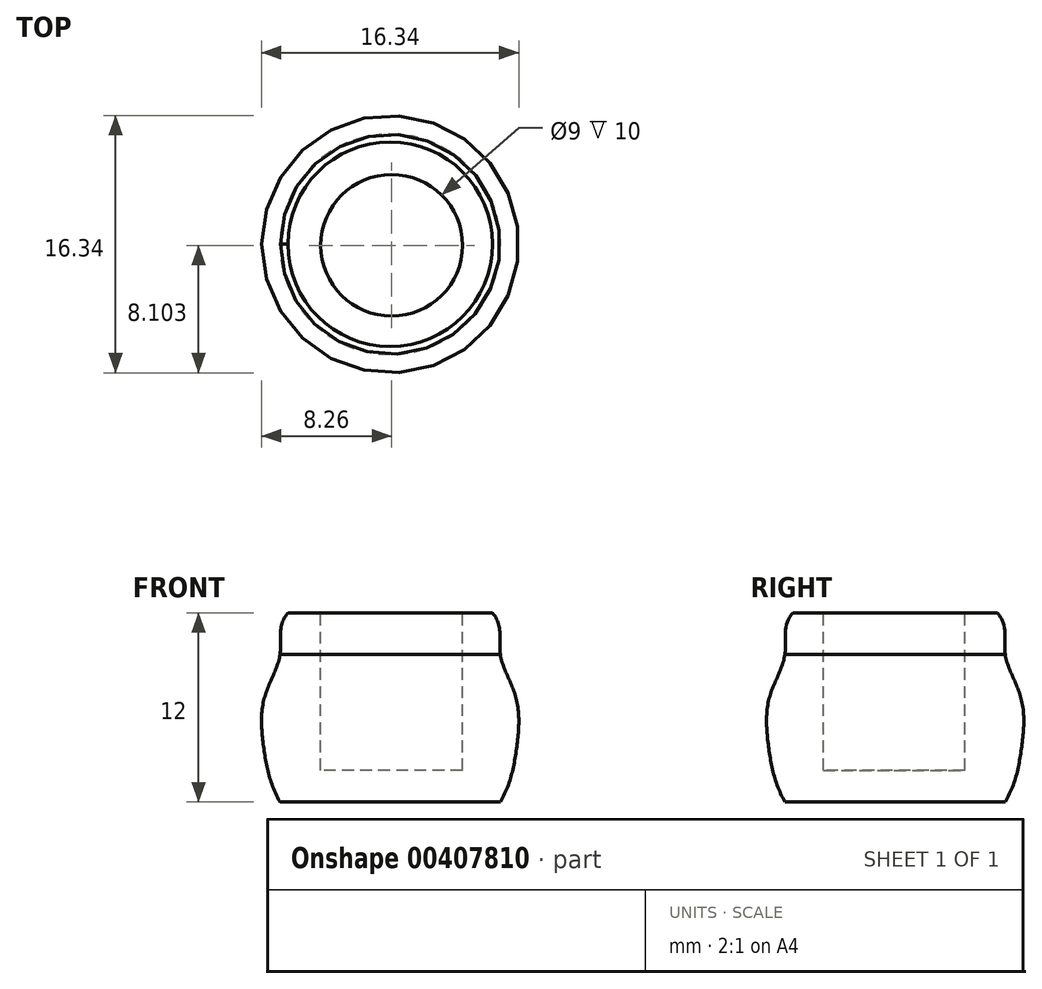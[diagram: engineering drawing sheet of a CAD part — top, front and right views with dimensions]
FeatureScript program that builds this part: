
annotation { "Feature Type Name" : "Feature", "Feature Type Description" : "" }
export const myFeature = defineFeature(function(context is Context, id is Id, definition is map)
    precondition{}
    {
        {
            var Q0;
            Q0=qCreatedBy(makeId("Front.planeOp"),FACE);
            var sketch = newSketch(context, id + "F0", { "sketchPlane" : qUnion([Q0])});
            skLineSegment(sketch, "E0", {"start": v(0, 0) * mm, "end": v(0, 12) * mm});
            skLineSegment(sketch, "E1", {"start": v(0, 0) * mm, "end": v(7, 0) * mm});
            skLineSegment(sketch, "E2", {"start": v(0, 12) * mm, "end": v(6.5, 12) * mm});
            skLineSegment(sketch, "E3", {"start": v(0, 6.58) * mm, "end": v(8, 6.58) * mm});
            skLineSegment(sketch, "E4", {"start": v(0, 3.23) * mm, "end": v(8, 3.23) * mm});
            skLineSegment(sketch, "E5", {"start": v(0, 9.37) * mm, "end": v(7, 9.37) * mm});
            skFitSpline(sketch, "E6", {"points": [v(6.5, 12) * mm, v(7, 9.37) * mm, v(8, 6.58) * mm, v(8, 3.23) * mm, v(7, 0) * mm], "startDerivative": vector(9.14, -10.6) * mm, "endDerivative": vector(-7.15, -12.58) * mm});
            skSolve(sketch);
        }
        {
            var Q0;
            Q0 = qSketchRegion(id + "F0", true);
            var Q1;
            Q1=sQuery(id+"F0.wireOp",EDGE,"E0");
            revolve(context, id + "F1", {"entities" : qUnion([Q0]), "axis" : qUnion([Q1]), "revolveType" : RevolveType.FULL});
        }
        {
            var Q0;
            Q0=makeQuery(id+"F1.opRevolve","SWEPT_FACE",FACE,{"disambiguationData":[OSD([sQuery(id+"F0.wireOp",EDGE,"E2")])]});
            var sketch = newSketch(context, id + "F2", { "sketchPlane" : qUnion([Q0])});
            skCircle(sketch, "E7", {"center": v(0.09, -0.07) * mm, "radius": 4.5 * mm});
            skSolve(sketch);
        }
        {
            var Q0;
            Q0 = qSketchRegion(id + "F2", true);
            extrude(context, id + "F3", {"entities" : qUnion([Q0]), "operationType" : NewBodyOperationType.REMOVE, "oppositeDirection" : true, "depth" : 10 * mm});
        }
    });
